# Revit family: Accessory-Robe_Hook-KOHLER-FAIRFAX-K-12156T
name_source: partatom
category: Specialty Equipment
revit_build: Autodesk Revit 2017 (Build: 20160225_1515(x64)
units: mm (PartAtom-declared; Revit-internal decimal feet)

## family parameters
Cut with Voids When Loaded = No
Host = Face
OmniClass Number = 23.31.25.27
OmniClass Title = Robe Hooks
Part Type = Normal
Room Calculation Point = No
Round Connector Dimension = Use Diameter
Shared = No

## types (3) — shared parameters
ADA Compliant = No
Assembly Code = C1030200
Date Modified = 06/16/2020
Default Elevation = 42"
Description = single hook
Height = 2 1/2"
Length = 3 5/8"
Manufacturer = KOHLER Co.
Master Format 2014 = 10 28 00
Master Format 2014 Name = Toilet, Bath, and Laundry Accessories
Material = Brass Construction
Product Documentation Link = https://files.kohler.com.cn
Product Name = FAIRFAX
Product Page URL = https://www.kohler.com.cn
URL = http://www.kohler.com.cn
WaterSense Certified = No
Width = 2 1/2"

## per-type parameters (varying)
| type | Finish | Model | Type |
| CP-Polished Chrome | Kohler-Metal-CP-Polished_Chrome | K-12156T-CP | 1 |
| BN-Roman Silver | Kohler-Metal-BN-Roman_Silver | K-12156T-BN | 2 |
| BV-Roman Copper | Kohler-Metal-BV-Roman_Copper | K-12156T-BV | 3 |

## geometry (parser evidence)
native form markers: Sweep x5
no freeform markers — native parametric forms only
